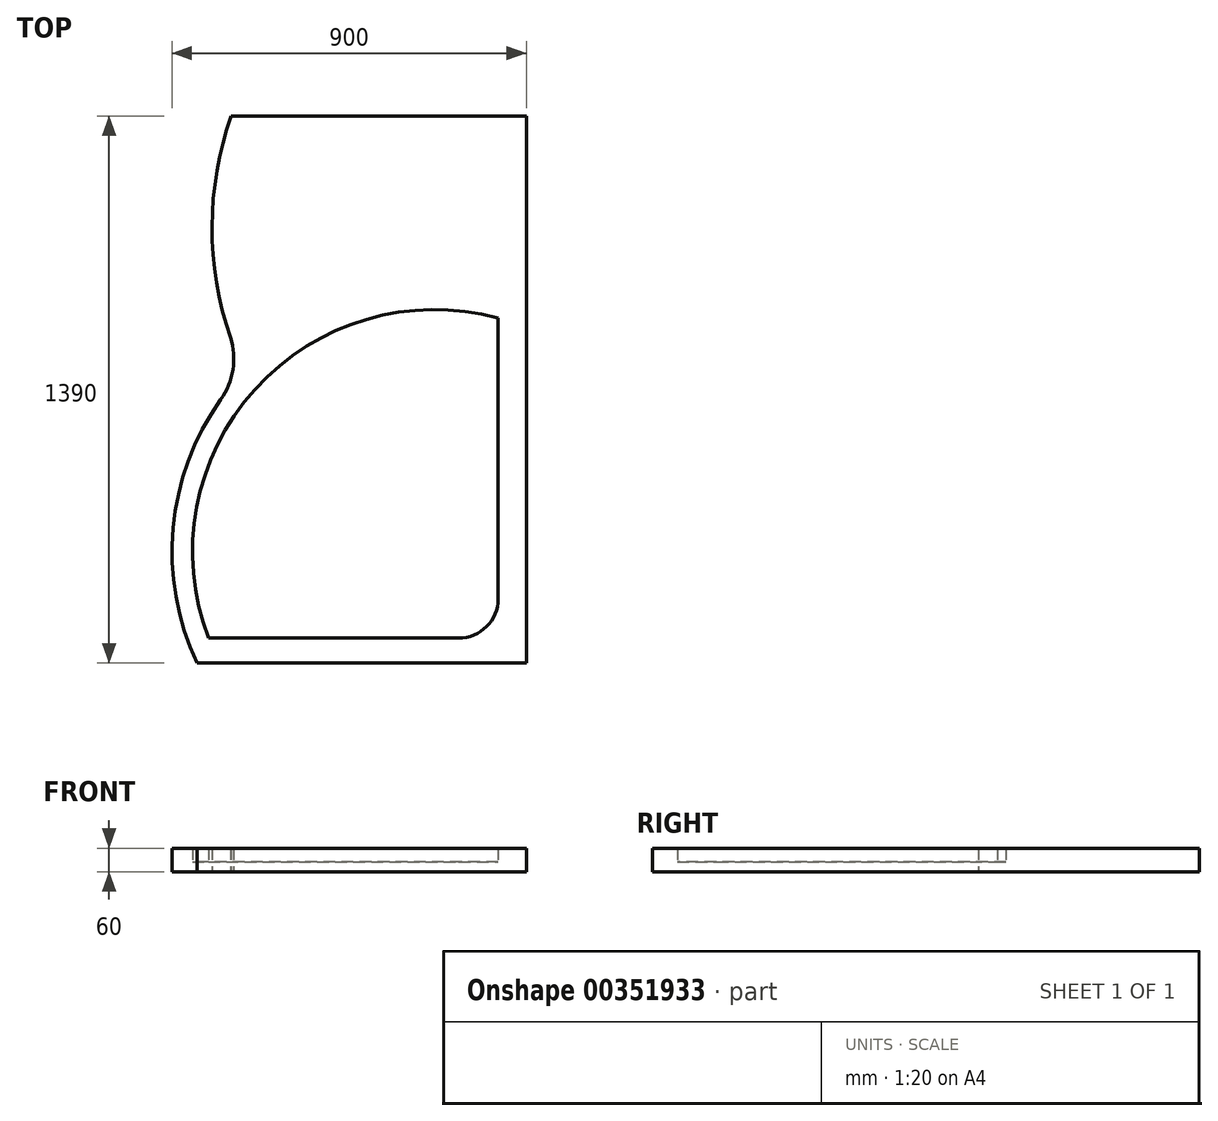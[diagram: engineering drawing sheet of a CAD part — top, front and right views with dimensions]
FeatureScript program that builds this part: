
annotation { "Feature Type Name" : "Feature", "Feature Type Description" : "" }
export const myFeature = defineFeature(function(context is Context, id is Id, definition is map)
    precondition{}
    {
        {
            var Q0;
            Q0=qCreatedBy(makeId("Top.planeOp"),FACE);
            var sketch = newSketch(context, id + "F0", { "sketchPlane" : qUnion([Q0])});
            skLineSegment(sketch, "E0", {"start": v(-365.47, -915.67) * mm, "end": v(471.53, -915.67) * mm});
            skLineSegment(sketch, "E1", {"start": v(471.53, -915.67) * mm, "end": v(471.53, 474.33) * mm});
            skLineSegment(sketch, "E2", {"start": v(471.53, 474.33) * mm, "end": v(-278.47, 474.33) * mm});
            skArc(sketch, "E3", {"start": v(-305.02, -246) * mm, "mid": v(-274, -169.74) * mm, "end": v(-280.37, -87.65) * mm});
            skArc(sketch, "E4.trimOffspring", {"start": v(-278.47, 474.33) * mm, "mid": v(-327, 193.5) * mm, "end": v(-280.37, -87.65) * mm});
            skArc(sketch, "E5", {"start": v(399.65, -38.58) * mm, "mid": v(-240.32, -246.24) * mm, "end": v(-307.8, -915.67) * mm});
            skLineSegment(sketch, "E6", {"start": v(-428.47, -301.13) * mm, "end": v(-428.47, -1050.99) * mm, "construction": true});
            skLineSegment(sketch, "E7", {"start": v(-336.3, -852.07) * mm, "end": v(299.65, -852.07) * mm});
            skLineSegment(sketch, "E8", {"start": v(-129.47, 174.9) * mm, "end": v(-129.47, -301.13) * mm, "construction": true});
            skLineSegment(sketch, "E9", {"start": v(399.65, -752.07) * mm, "end": v(399.65, 313.21) * mm});
            skLineSegment(sketch, "E10", {"start": v(299.65, 413.21) * mm, "end": v(-158.27, 413.21) * mm});
            skArc(sketch, "E11.trimOffspring", {"start": v(-305.02, -246) * mm, "mid": v(-425.77, -572.67) * mm, "end": v(-365.47, -915.67) * mm});
            skLineSegment(sketch, "E12", {"start": v(171.53, -255.67) * mm, "end": v(471.53, -255.67) * mm});
            skPoint(sketch, "E13.visualSharp", {"position": v(399.65, -852.07) * mm});
            skArc(sketch, "E13.filletArc", {"start": v(299.65, -852.07) * mm, "mid": v(370.36, -822.78) * mm, "end": v(399.65, -752.07) * mm});
            skPoint(sketch, "E14.visualSharp", {"position": v(399.65, 413.21) * mm});
            skArc(sketch, "E14.filletArc", {"start": v(399.65, 313.21) * mm, "mid": v(370.36, 383.92) * mm, "end": v(299.65, 413.21) * mm});
            skArc(sketch, "E15.trimOffspring", {"start": v(-129.47, -106.5) * mm, "mid": v(-383.19, -472.58) * mm, "end": v(-337.73, -915.67) * mm});
            skLineSegment(sketch, "E16", {"start": v(-249.47, 474.33) * mm, "end": v(-249.47, 174.33) * mm});
            skArc(sketch, "E17", {"start": v(-249.47, 174.33) * mm, "mid": v(-118.29, -118.33) * mm, "end": v(171.53, -255.67) * mm});
            skSolve(sketch);
        }
        {
            var Q0;
            Q0 = qSketchRegion(id + "F0", true);
            extrude(context, id + "F1", {"entities" : qUnion([Q0]), "depth" : 60 * mm});
        }
        {
            var Q0;
            {var subQ6=sQuery(id+"F0.wireOp",EDGE,"E7");Q0=makeQuery(id+"F0.imprint","IMPRINT",FACE,{"disambiguationData":[TD([[makeQuery(id+"F0.imprint","IMPRINT",EDGE,{"derivedFrom":subQ6}),1.0]])]});}
            var Q1;
            {var subQ0=sQuery(id+"F0.wireOp",EDGE,"E9");var subQ1=sQuery(id+"F0.wireOp",EDGE,"E5");var subQ2=makeQuery(id+"F0.imprint","INTERSECT",VERTEX,{"derivedFrom":[subQ1,subQ0]});Q1=makeQuery(id+"F0.imprint","IMPRINT",FACE,{"disambiguationData":[TD([[makeQuery(id+"F0.imprint","IMPRINT",EDGE,{"disambiguationData":[TD([[subQ2,-1.0]])],"derivedFrom":subQ1}),1.0]])]});}
            extrude(context, id + "F2", {"entities" : qUnion([Q0, Q1]), "operationType" : NewBodyOperationType.ADD, "depth" : 25 * mm});
        }
        {
            var Q0;
            Q0=sQuery(id+"F0.wireOp",EDGE,"E15.trimOffspring");
            extrude(context, id + "F3", {"bodyType" : ToolBodyType.SURFACE, "surfaceEntities" : qUnion([Q0]), "depth" : 1850 * mm});
        }
        {
            var Q0;
            Q0=sQuery(id+"F0.wireOp",EDGE,"E12");
            var Q1;
            Q1=sQuery(id+"F0.wireOp",EDGE,"E17");
            var Q2;
            Q2=sQuery(id+"F0.wireOp",EDGE,"E16");
            extrude(context, id + "F4", {"bodyType" : ToolBodyType.SURFACE, "surfaceEntities" : qUnion([Q0, Q1, Q2]), "depth" : 1940 * mm, "hasSecondDirection" : true, "secondDirectionOppositeDirection" : false, "secondDirectionDepth" : 1850 * mm});
        }
    });
